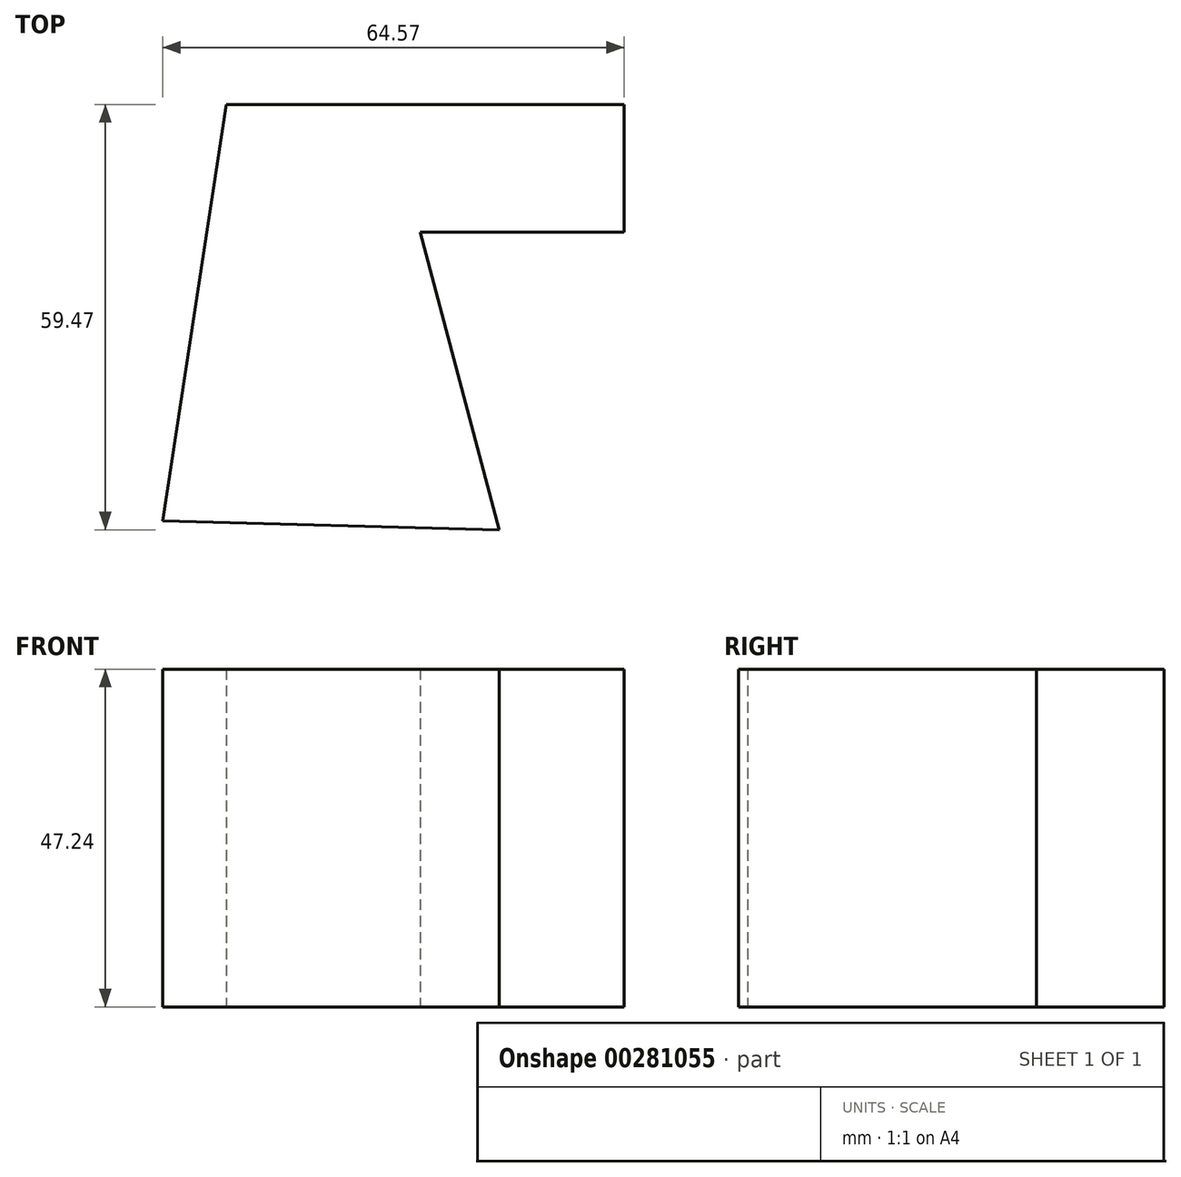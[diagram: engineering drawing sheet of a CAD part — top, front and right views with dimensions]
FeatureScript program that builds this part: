
annotation { "Feature Type Name" : "Feature", "Feature Type Description" : "" }
export const myFeature = defineFeature(function(context is Context, id is Id, definition is map)
    precondition{}
    {
        {
            var Q0;
            Q0=qCreatedBy(makeId("Top.planeOp"),FACE);
            var sketch = newSketch(context, id + "F0", { "sketchPlane" : qUnion([Q0])});
            skLineSegment(sketch, "E0", {"start": v(-47.06, -34.09) * mm, "end": v(-38.15, 24.14) * mm});
            skLineSegment(sketch, "E1", {"start": v(-38.15, 24.14) * mm, "end": v(-15.78, 24.14) * mm});
            skLineSegment(sketch, "E2", {"start": v(-15.78, 24.14) * mm, "end": v(0, -35.33) * mm});
            skLineSegment(sketch, "E3", {"start": v(0, -35.33) * mm, "end": v(-47.06, -34.09) * mm});
            skLineSegment(sketch, "E4", {"start": v(-15.78, 24.14) * mm, "end": v(17.51, 24.14) * mm});
            skLineSegment(sketch, "E5", {"start": v(17.51, 24.14) * mm, "end": v(17.51, 6.32) * mm});
            skLineSegment(sketch, "E6", {"start": v(17.51, 6.32) * mm, "end": v(-11.05, 6.32) * mm});
            skSolve(sketch);
        }
        {
            var Q0;
            {var subQ0=sQuery(id+"F0.wireOp",EDGE,"E4");Q0=makeQuery(id+"F0.imprint","IMPRINT",FACE,{"disambiguationData":[TD([[makeQuery(id+"F0.imprint","IMPRINT",EDGE,{"derivedFrom":subQ0}),-1.0]])]});}
            var Q1;
            Q1=makeQuery(id+"F0.imprint","IMPRINT",FACE,{"disambiguationData":[TD([[makeQuery(id+"F0.imprint","IMPRINT",EDGE,{"derivedFrom":sQuery(id+"F0.wireOp",EDGE,"E0")}),-1.0]])]});
            extrude(context, id + "F1", {"entities" : qUnion([Q0, Q1]), "depth" : 47.24 * mm});
        }
    });
